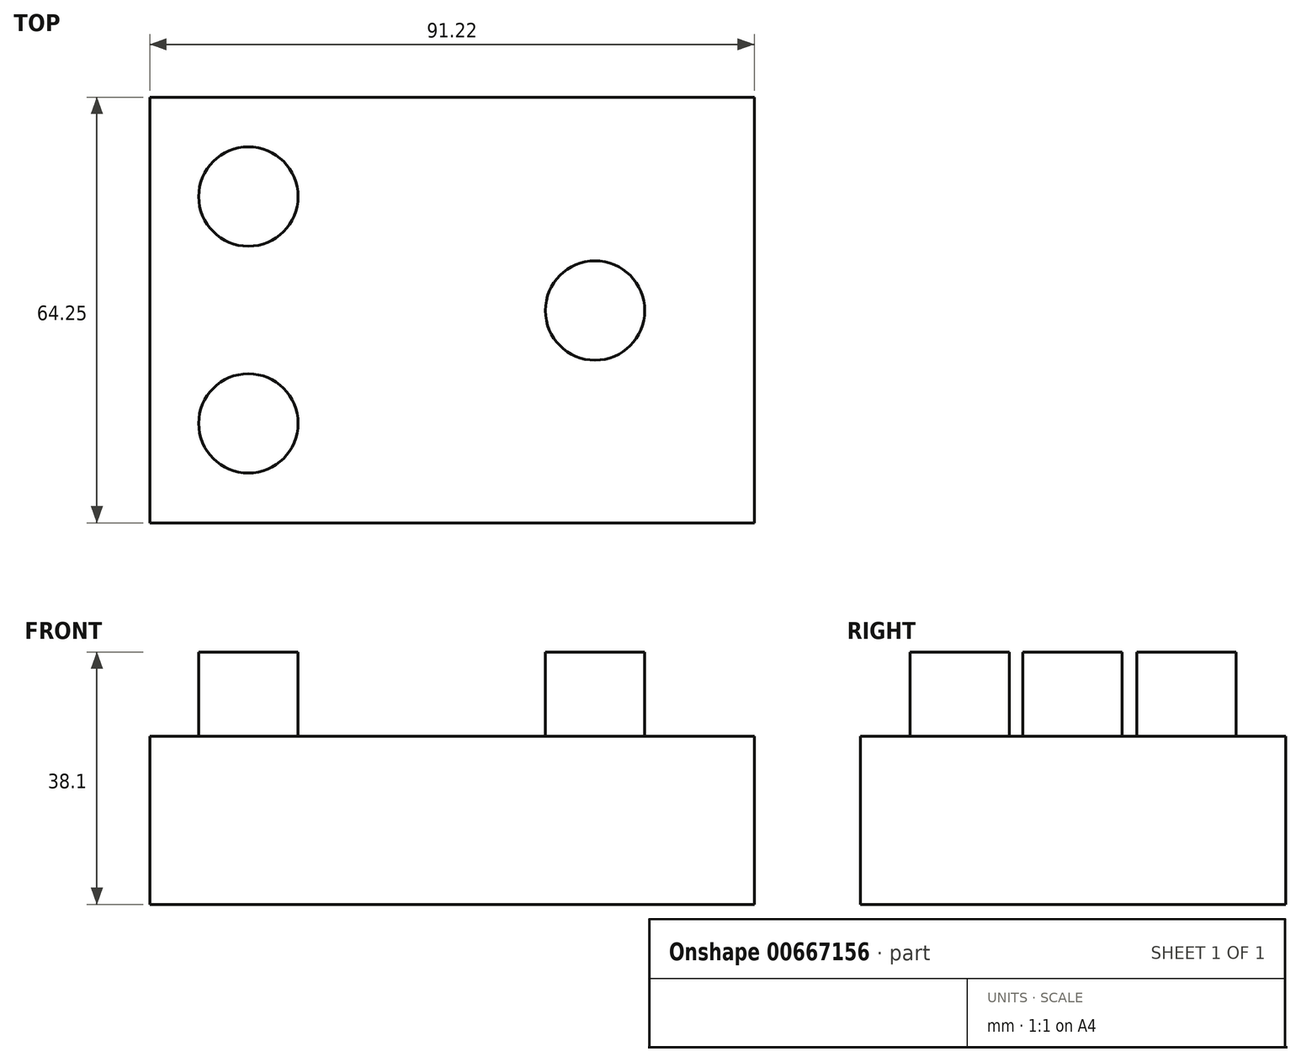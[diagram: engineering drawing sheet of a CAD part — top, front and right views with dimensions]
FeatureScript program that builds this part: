
annotation { "Feature Type Name" : "Feature", "Feature Type Description" : "" }
export const myFeature = defineFeature(function(context is Context, id is Id, definition is map)
    precondition{}
    {
        {
            var Q0;
            Q0=qCreatedBy(makeId("Top.planeOp"),FACE);
            var sketch = newSketch(context, id + "F0", { "sketchPlane" : qUnion([Q0])});
            skLineSegment(sketch, "E0.bottom", {"start": v(-42.53, 32.21) * mm, "end": v(48.7, 32.21) * mm});
            skLineSegment(sketch, "E0.top", {"start": v(-42.53, -32.04) * mm, "end": v(48.7, -32.04) * mm});
            skLineSegment(sketch, "E0.left", {"start": v(-42.53, 32.21) * mm, "end": v(-42.53, -32.04) * mm});
            skLineSegment(sketch, "E0.right", {"start": v(48.7, 32.21) * mm, "end": v(48.7, -32.04) * mm});
            skSolve(sketch);
        }
        {
            var Q0;
            Q0 = qSketchRegion(id + "F0", true);
            extrude(context, id + "F1", {"entities" : qUnion([Q0]), "depth" : 25.4 * mm, "offsetDistance" : 25.4 * mm});
        }
        {
            var Q0;
            Q0=makeQuery(id+"F1.opExtrude","CAP_FACE",FACE,{"disambiguationData":[OSD([sQuery(id+"F0.wireOp",EDGE,"E0.bottom"),sQuery(id+"F0.wireOp",EDGE,"E0.top"),sQuery(id+"F0.wireOp",EDGE,"E0.left"),sQuery(id+"F0.wireOp",EDGE,"E0.right")])],"isStart":false});
            var sketch = newSketch(context, id + "F2", { "sketchPlane" : qUnion([Q0])});
            skCircle(sketch, "E1", {"center": v(-27.67, 17.21) * mm, "radius": 7.5 * mm});
            skCircle(sketch, "E2", {"center": v(-27.67, -17.04) * mm, "radius": 7.5 * mm});
            skCircle(sketch, "E3", {"center": v(24.67, 0) * mm, "radius": 7.5 * mm});
            skSolve(sketch);
        }
        {
            var Q0;
            Q0 = qSketchRegion(id + "F2", true);
            extrude(context, id + "F3", {"entities" : qUnion([Q0]), "operationType" : NewBodyOperationType.ADD, "depth" : 12.7 * mm, "offsetDistance" : 25.4 * mm});
        }
    });
